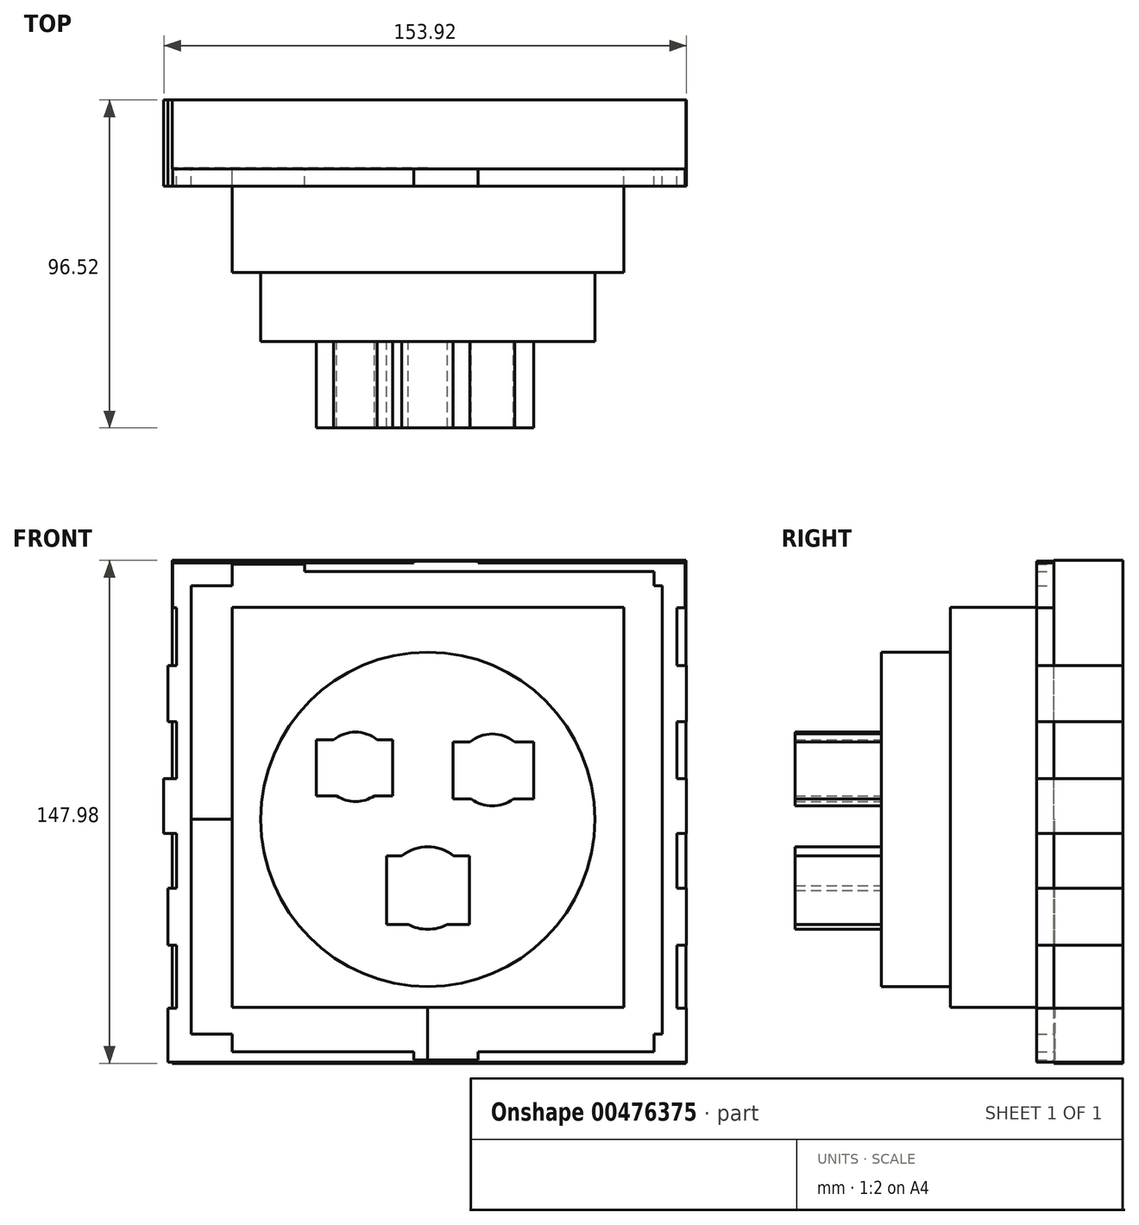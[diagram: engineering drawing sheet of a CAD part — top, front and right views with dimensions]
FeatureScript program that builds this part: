
annotation { "Feature Type Name" : "Feature", "Feature Type Description" : "" }
export const myFeature = defineFeature(function(context is Context, id is Id, definition is map)
    precondition{}
    {
        {
            var Q0;
            Q0=qCreatedBy(makeId("Front.planeOp"),FACE);
            var sketch = newSketch(context, id + "F0", { "sketchPlane" : qUnion([Q0])});
            skLineSegment(sketch, "E0.bottom", {"start": v(-76.5, 45.26) * mm, "end": v(76.2, 45.26) * mm});
            skLineSegment(sketch, "E0.top", {"start": v(-76.5, 28.8) * mm, "end": v(76.2, 28.8) * mm});
            skLineSegment(sketch, "E0.left", {"start": v(-76.5, 45.26) * mm, "end": v(-76.5, 28.8) * mm});
            skLineSegment(sketch, "E0.right", {"start": v(76.2, 45.26) * mm, "end": v(76.2, 28.8) * mm});
            skLineSegment(sketch, "E1.bottom", {"start": v(-77.72, 12.04) * mm, "end": v(76.2, 12.04) * mm});
            skLineSegment(sketch, "E1.top", {"start": v(-77.72, -4.11) * mm, "end": v(76.2, -4.11) * mm});
            skLineSegment(sketch, "E1.left", {"start": v(-77.72, 12.04) * mm, "end": v(-77.72, -4.11) * mm});
            skLineSegment(sketch, "E1.right", {"start": v(76.2, 12.04) * mm, "end": v(76.2, -4.11) * mm});
            skLineSegment(sketch, "E2.bottom", {"start": v(-76.5, -20.27) * mm, "end": v(76.2, -20.27) * mm});
            skLineSegment(sketch, "E2.top", {"start": v(-76.5, -37.03) * mm, "end": v(76.2, -37.03) * mm});
            skLineSegment(sketch, "E2.left", {"start": v(-76.5, -20.27) * mm, "end": v(-76.5, -37.03) * mm});
            skLineSegment(sketch, "E2.right", {"start": v(76.2, -20.27) * mm, "end": v(76.2, -37.03) * mm});
            skLineSegment(sketch, "E3.bottom", {"start": v(-76.5, -55.63) * mm, "end": v(76.2, -55.63) * mm});
            skLineSegment(sketch, "E3.top", {"start": v(-76.5, -71.48) * mm, "end": v(76.2, -71.48) * mm});
            skLineSegment(sketch, "E3.left", {"start": v(-76.5, -55.63) * mm, "end": v(-76.5, -71.48) * mm});
            skLineSegment(sketch, "E3.right", {"start": v(76.2, -55.63) * mm, "end": v(76.2, -71.48) * mm});
            skLineSegment(sketch, "E4.bottom", {"start": v(-57.6, 75.13) * mm, "end": v(-36.27, 75.13) * mm});
            skLineSegment(sketch, "E4.top", {"start": v(-57.6, -71.48) * mm, "end": v(-36.27, -71.48) * mm});
            skLineSegment(sketch, "E4.left", {"start": v(-57.6, 75.13) * mm, "end": v(-57.6, -71.48) * mm});
            skLineSegment(sketch, "E4.right", {"start": v(-36.27, 75.13) * mm, "end": v(-36.27, -71.48) * mm});
            skLineSegment(sketch, "E5.bottom", {"start": v(-4.11, -70.87) * mm, "end": v(14.78, -70.87) * mm});
            skLineSegment(sketch, "E5.top", {"start": v(-4.11, 76.05) * mm, "end": v(14.78, 76.05) * mm});
            skLineSegment(sketch, "E5.left", {"start": v(-4.11, -70.87) * mm, "end": v(-4.11, 76.05) * mm});
            skLineSegment(sketch, "E5.right", {"start": v(14.78, -70.87) * mm, "end": v(14.78, 76.05) * mm});
            skLineSegment(sketch, "E6.bottom", {"start": v(49.53, -71.48) * mm, "end": v(66.6, -71.48) * mm});
            skLineSegment(sketch, "E6.top", {"start": v(49.53, 75.44) * mm, "end": v(66.6, 75.44) * mm});
            skLineSegment(sketch, "E6.left", {"start": v(49.53, -71.48) * mm, "end": v(49.53, 75.44) * mm});
            skLineSegment(sketch, "E6.right", {"start": v(66.6, -71.48) * mm, "end": v(66.6, 75.44) * mm});
            skLineSegment(sketch, "E7.bottom", {"start": v(-75.13, 62.33) * mm, "end": v(75.74, 62.33) * mm});
            skLineSegment(sketch, "E7.top", {"start": v(-75.13, 75.44) * mm, "end": v(75.74, 75.44) * mm});
            skLineSegment(sketch, "E7.left", {"start": v(-75.13, 62.33) * mm, "end": v(-75.13, 75.44) * mm});
            skLineSegment(sketch, "E7.right", {"start": v(75.74, 62.33) * mm, "end": v(75.74, 75.44) * mm});
            skLineSegment(sketch, "E8.bottom", {"start": v(73.3, 73) * mm, "end": v(-73.91, 73) * mm});
            skLineSegment(sketch, "E8.top", {"start": v(73.3, -68.43) * mm, "end": v(-73.91, -68.43) * mm});
            skLineSegment(sketch, "E8.left", {"start": v(73.3, 73) * mm, "end": v(73.3, -68.43) * mm});
            skLineSegment(sketch, "E8.right", {"start": v(-73.91, 73) * mm, "end": v(-73.91, -68.43) * mm});
            skLineSegment(sketch, "E9.bottom", {"start": v(69.04, 68.73) * mm, "end": v(-69.65, 68.73) * mm});
            skLineSegment(sketch, "E9.top", {"start": v(69.04, -63.25) * mm, "end": v(-69.65, -63.25) * mm});
            skLineSegment(sketch, "E9.left", {"start": v(69.04, 68.73) * mm, "end": v(69.04, -63.25) * mm});
            skLineSegment(sketch, "E9.right", {"start": v(-69.65, 68.73) * mm, "end": v(-69.65, -63.25) * mm});
            skCircle(sketch, "E10", {"center": v(45.57, 56.54) * mm, "radius": 3.05 * mm});
            skCircle(sketch, "E11", {"center": v(17.83, 56.54) * mm, "radius": 3.05 * mm});
            skCircle(sketch, "E12", {"center": v(-9, 56.24) * mm, "radius": 3.05 * mm});
            skCircle(sketch, "E13", {"center": v(-31.55, 56.24) * mm, "radius": 3 * mm});
            skCircle(sketch, "E14", {"center": v(-49.23, 55.93) * mm, "radius": 3.18 * mm});
            skCircle(sketch, "E15", {"center": v(45.57, 19.66) * mm, "radius": 3.28 * mm});
            skCircle(sketch, "E16", {"center": v(18.14, 19.35) * mm, "radius": 3.35 * mm});
            skCircle(sketch, "E17", {"center": v(-8.38, 19.66) * mm, "radius": 3.18 * mm});
            skCircle(sketch, "E18", {"center": v(-29.1, 19.05) * mm, "radius": 3.24 * mm});
            skCircle(sketch, "E19", {"center": v(-51.97, 17.83) * mm, "radius": 3.1 * mm});
            skCircle(sketch, "E20", {"center": v(46.18, -12.95) * mm, "radius": 3.14 * mm});
            skCircle(sketch, "E21", {"center": v(19.66, -12.95) * mm, "radius": 2.6 * mm});
            skCircle(sketch, "E22", {"center": v(-8.69, -12.65) * mm, "radius": 3 * mm});
            skCircle(sketch, "E23", {"center": v(-30.94, -13.26) * mm, "radius": 3.24 * mm});
            skCircle(sketch, "E24", {"center": v(-54.1, -12.95) * mm, "radius": 3.5 * mm});
            skCircle(sketch, "E25", {"center": v(46.48, -46.18) * mm, "radius": 2.81 * mm});
            skCircle(sketch, "E26", {"center": v(20.57, -46.48) * mm, "radius": 3.06 * mm});
            skCircle(sketch, "E27", {"center": v(-9.3, -46.79) * mm, "radius": 3.18 * mm});
            skCircle(sketch, "E28", {"center": v(-30.94, -47.4) * mm, "radius": 3.05 * mm});
            skCircle(sketch, "E29", {"center": v(-51.66, -47.7) * mm, "radius": 3.14 * mm});
            skSolve(sketch);
        }
        {
            var Q0;
            Q0=qCreatedBy(makeId("Front.planeOp"),FACE);
            var sketch = newSketch(context, id + "F1", { "sketchPlane" : qUnion([Q0])});
            skLineSegment(sketch, "E30.bottom", {"start": v(-75.28, 76.2) * mm, "end": v(76.05, 76.2) * mm});
            skLineSegment(sketch, "E30.top", {"start": v(-75.28, -71.78) * mm, "end": v(76.05, -71.78) * mm});
            skLineSegment(sketch, "E30.left", {"start": v(-75.28, 76.2) * mm, "end": v(-75.28, -71.78) * mm});
            skLineSegment(sketch, "E30.right", {"start": v(76.05, 76.2) * mm, "end": v(76.05, -71.78) * mm});
            skSolve(sketch);
        }
        {
            var Q0;
            Q0=qSketchRegion(id+"F1",true);
            extrude(context, id + "F2", {"entities" : qUnion([Q0]), "depth" : 20.07 * mm});
        }
        {
            var Q0;
            Q0=makeQuery(id+"F2.opExtrude","CAP_FACE",FACE,{"disambiguationData":[OSD([sQuery(id+"F1.wireOp",EDGE,"E30.bottom"),sQuery(id+"F1.wireOp",EDGE,"E30.top"),sQuery(id+"F1.wireOp",EDGE,"E30.left"),sQuery(id+"F1.wireOp",EDGE,"E30.right")])],"isStart":false});
            var sketch = newSketch(context, id + "F3", { "sketchPlane" : qUnion([Q0])});
            skLineSegment(sketch, "E31.bottom", {"start": v(-75.28, 76.2) * mm, "end": v(0, 76.2) * mm});
            skLineSegment(sketch, "E31.top", {"start": v(-75.28, 0) * mm, "end": v(0, 0) * mm});
            skLineSegment(sketch, "E31.left", {"start": v(-75.28, 76.2) * mm, "end": v(-75.28, 0) * mm});
            skLineSegment(sketch, "E31.right", {"start": v(0, 76.2) * mm, "end": v(0, 0) * mm});
            skLineSegment(sketch, "E32.bottom", {"start": v(0, 0) * mm, "end": v(76.05, 0) * mm});
            skLineSegment(sketch, "E32.top", {"start": v(0, 76.2) * mm, "end": v(76.05, 76.2) * mm});
            skLineSegment(sketch, "E32.left", {"start": v(0, 0) * mm, "end": v(0, 76.2) * mm});
            skLineSegment(sketch, "E32.right", {"start": v(76.05, 0) * mm, "end": v(76.05, 76.2) * mm});
            skLineSegment(sketch, "E33.bottom", {"start": v(0, 0) * mm, "end": v(-75.28, 0) * mm});
            skLineSegment(sketch, "E33.top", {"start": v(0, -71.78) * mm, "end": v(-75.28, -71.78) * mm});
            skLineSegment(sketch, "E33.left", {"start": v(0, 0) * mm, "end": v(0, -71.78) * mm});
            skLineSegment(sketch, "E33.right", {"start": v(-75.28, 0) * mm, "end": v(-75.28, -71.78) * mm});
            skLineSegment(sketch, "E34.top", {"start": v(0, -71.78) * mm, "end": v(76.05, -71.78) * mm});
            skLineSegment(sketch, "E34.right", {"start": v(76.05, 0) * mm, "end": v(76.05, -71.78) * mm});
            skSolve(sketch);
        }
        {
            var Q0;
            Q0=makeQuery(id+"F3.imprint","IMPRINT",FACE,{"disambiguationData":[TD([[makeQuery(id+"F3.imprint","IMPRINT",EDGE,{"derivedFrom":sQuery(id+"F3.wireOp",EDGE,"E31.bottom")}),-1.0]])]});
            var Q1;
            Q1=makeQuery(id+"F3.imprint","IMPRINT",FACE,{"disambiguationData":[TD([[makeQuery(id+"F3.imprint","IMPRINT",EDGE,{"derivedFrom":sQuery(id+"F3.wireOp",EDGE,"E33.bottom")}),1.0]])]});
            var Q2;
            Q2=makeQuery(id+"F3.imprint","IMPRINT",FACE,{"disambiguationData":[TD([[makeQuery(id+"F3.imprint","IMPRINT",EDGE,{"derivedFrom":sQuery(id+"F3.wireOp",EDGE,"E32.bottom")}),-1.0]])]});
            var Q3;
            Q3=makeQuery(id+"F3.imprint","IMPRINT",FACE,{"disambiguationData":[TD([[makeQuery(id+"F3.imprint","IMPRINT",EDGE,{"derivedFrom":sQuery(id+"F3.wireOp",EDGE,"E32.top")}),-1.0]])]});
            extrude(context, id + "F4", {"entities" : qUnion([Q0, Q1, Q2, Q3]), "operationType" : NewBodyOperationType.ADD, "depth" : 0.25 * mm});
        }
        {
            var Q0;
            Q0=makeQuery(id+"F4.opExtrude","CAP_FACE",FACE,{"disambiguationData":[OSD([sQuery(id+"F3.wireOp",EDGE,"E31.bottom"),sQuery(id+"F3.wireOp",EDGE,"E31.left"),sQuery(id+"F3.wireOp",EDGE,"E32.top"),sQuery(id+"F3.wireOp",EDGE,"E32.right"),sQuery(id+"F3.wireOp",EDGE,"E33.top"),sQuery(id+"F3.wireOp",EDGE,"E33.right"),sQuery(id+"F3.wireOp",EDGE,"E34.top"),sQuery(id+"F3.wireOp",EDGE,"E34.right")])],"isStart":false});
            var sketch = newSketch(context, id + "F5", { "sketchPlane" : qUnion([Q0])});
            skCircle(sketch, "E35", {"center": v(0, 0) * mm, "radius": 49.2 * mm});
            skSolve(sketch);
        }
        {
            var Q0;
            Q0=qSketchRegion(id+"F5",true);
            extrude(context, id + "F6", {"entities" : qUnion([Q0]), "operationType" : NewBodyOperationType.ADD, "depth" : 25.4 * mm});
        }
        {
            var Q0;
            Q0=makeQuery(id+"F6.opExtrude","CAP_FACE",FACE,{"disambiguationData":[OSD([sQuery(id+"F5.wireOp",EDGE,"E35")])],"isStart":false});
            var sketch = newSketch(context, id + "F7", { "sketchPlane" : qUnion([Q0])});
            skArc(sketch, "E36", {"start": v(-52.7, 45.38) * mm, "mid": v(52.15, -40.45) * mm, "end": v(-51.18, 47.21) * mm});
            skSolve(sketch);
        }
        {
            var Q0;
            Q0=makeQuery(id+"F7.imprint","IMPRINT",FACE,{"disambiguationData":[TD([[makeQuery(id+"F7.imprint","IMPRINT",EDGE,{"derivedFrom":makeQuery(id+"F6.opExtrude","CAP_EDGE",EDGE,{"disambiguationData":[OSD([sQuery(id+"F5.wireOp",EDGE,"E35")])],"isStart":false})}),1.0]])]});
            extrude(context, id + "F8", {"entities" : qUnion([Q0]), "operationType" : NewBodyOperationType.ADD, "depth" : 25.4 * mm});
        }
        {
            var Q0;
            Q0=makeQuery(id+"F4.opExtrude","CAP_FACE",FACE,{"disambiguationData":[OSD([sQuery(id+"F3.wireOp",EDGE,"E31.bottom"),sQuery(id+"F3.wireOp",EDGE,"E31.left"),sQuery(id+"F3.wireOp",EDGE,"E32.top"),sQuery(id+"F3.wireOp",EDGE,"E32.right"),sQuery(id+"F3.wireOp",EDGE,"E33.top"),sQuery(id+"F3.wireOp",EDGE,"E33.right"),sQuery(id+"F3.wireOp",EDGE,"E34.top"),sQuery(id+"F3.wireOp",EDGE,"E34.right")])],"isStart":false});
            var sketch = newSketch(context, id + "F9", { "sketchPlane" : qUnion([Q0])});
            skCircle(sketch, "E37", {"center": v(0, 0) * mm, "radius": 70.77 * mm});
            skSolve(sketch);
        }
        {
            var Q0;
            Q0=qCreatedBy(makeId("Front.planeOp"),FACE);
            var sketch = newSketch(context, id + "F10", { "sketchPlane" : qUnion([Q0])});
            skCircle(sketch, "E38", {"center": v(45.23, 56.98) * mm, "radius": 3.19 * mm});
            skCircle(sketch, "E39", {"center": v(18.08, 56.67) * mm, "radius": 3.48 * mm});
            skCircle(sketch, "E40", {"center": v(-8.77, 56.67) * mm, "radius": 3.56 * mm});
            skCircle(sketch, "E41", {"center": v(-31.65, 56.67) * mm, "radius": 2.88 * mm});
            skCircle(sketch, "E42", {"center": v(-49.35, 56.67) * mm, "radius": 2.46 * mm});
            skCircle(sketch, "E43", {"center": v(45.84, 20.06) * mm, "radius": 3.37 * mm});
            skCircle(sketch, "E44", {"center": v(18.08, 19.15) * mm, "radius": 3.48 * mm});
            skCircle(sketch, "E45", {"center": v(-8.16, 20.06) * mm, "radius": 3.11 * mm});
            skCircle(sketch, "E46", {"center": v(-28.9, 19.15) * mm, "radius": 3.14 * mm});
            skCircle(sketch, "E47", {"center": v(-52.4, 18.23) * mm, "radius": 3.24 * mm});
            skCircle(sketch, "E48", {"center": v(46.45, -12.9) * mm, "radius": 3.57 * mm});
            skCircle(sketch, "E49", {"center": v(19.6, -12.59) * mm, "radius": 2.62 * mm});
            skCircle(sketch, "E50", {"center": v(-8.47, -12.59) * mm, "radius": 3.37 * mm});
            skCircle(sketch, "E51", {"center": v(-31.04, -13.2) * mm, "radius": 3.48 * mm});
            skCircle(sketch, "E52", {"center": v(-52.4, -12.28) * mm, "radius": 3.48 * mm});
            skCircle(sketch, "E53", {"center": v(46.45, -45.84) * mm, "radius": 3.41 * mm});
            skCircle(sketch, "E54", {"center": v(20.52, -45.54) * mm, "radius": 2.73 * mm});
            skCircle(sketch, "E55", {"center": v(-10.3, -46.76) * mm, "radius": 3.3 * mm});
            skCircle(sketch, "E56", {"center": v(-31.65, -47.06) * mm, "radius": 4.01 * mm});
            skCircle(sketch, "E57", {"center": v(-52.4, -47.37) * mm, "radius": 3.48 * mm});
            skSolve(sketch);
        }
        {
            var Q0;
            Q0=qSketchRegion(id+"F10",true);
            extrude(context, id + "F11", {"entities" : qUnion([Q0]), "operationType" : NewBodyOperationType.ADD, "depth" : 25.4 * mm});
        }
        {
            var Q0;
            Q0=qSketchRegion(id+"F0",true);
            extrude(context, id + "F12", {"entities" : qUnion([Q0]), "operationType" : NewBodyOperationType.ADD, "depth" : 25.4 * mm});
        }
        {
            var Q0;
            Q0=qCreatedBy(makeId("Front.planeOp"),FACE);
            var sketch = newSketch(context, id + "F13", { "sketchPlane" : qUnion([Q0])});
            skLineSegment(sketch, "E58.bottom", {"start": v(-57.59, 62.47) * mm, "end": v(57.74, 62.47) * mm});
            skLineSegment(sketch, "E58.top", {"start": v(-57.59, -55.3) * mm, "end": v(57.74, -55.3) * mm});
            skLineSegment(sketch, "E58.left", {"start": v(-57.59, 62.47) * mm, "end": v(-57.59, -55.3) * mm});
            skLineSegment(sketch, "E58.right", {"start": v(57.74, 62.47) * mm, "end": v(57.74, -55.3) * mm});
            skSolve(sketch);
        }
        {
            var Q0;
            Q0=qSketchRegion(id+"F13",true);
            extrude(context, id + "F14", {"entities" : qUnion([Q0]), "operationType" : NewBodyOperationType.ADD, "depth" : 50.8 * mm});
        }
        {
            var Q0;
            Q0=makeQuery(id+"F8.opExtrude","CAP_FACE",FACE,{"disambiguationData":[OSD([sQuery(id+"F5.wireOp",EDGE,"E35")])],"isStart":false});
            var sketch = newSketch(context, id + "F15", { "sketchPlane" : qUnion([Q0])});
            skCircle(sketch, "E59", {"center": v(-21.28, 15.48) * mm, "radius": 10.2 * mm});
            skCircle(sketch, "E60", {"center": v(19, 14.57) * mm, "radius": 10.57 * mm});
            skCircle(sketch, "E61", {"center": v(0, -20.21) * mm, "radius": 12.15 * mm});
            skSolve(sketch);
        }
        {
            var Q0;
            Q0 = qSketchRegion(id + "F15", true);
            extrude(context, id + "F16", {"entities" : qUnion([Q0]), "operationType" : NewBodyOperationType.ADD, "depth" : 25.4 * mm});
        }
        {
            var Q0;
            Q0=makeQuery(id+"F8.opExtrude","CAP_FACE",FACE,{"disambiguationData":[OSD([sQuery(id+"F5.wireOp",EDGE,"E35")])],"isStart":false});
            var sketch = newSketch(context, id + "F17", { "sketchPlane" : qUnion([Q0])});
            skLineSegment(sketch, "E62.bottom", {"start": v(-32.87, 23.42) * mm, "end": v(-10.3, 23.42) * mm});
            skLineSegment(sketch, "E62.top", {"start": v(-32.87, 6.94) * mm, "end": v(-10.3, 6.94) * mm});
            skLineSegment(sketch, "E62.left", {"start": v(-32.87, 23.42) * mm, "end": v(-32.87, 6.94) * mm});
            skLineSegment(sketch, "E62.right", {"start": v(-10.3, 23.42) * mm, "end": v(-10.3, 6.94) * mm});
            skLineSegment(sketch, "E63.bottom", {"start": v(7.4, 22.8) * mm, "end": v(31.2, 22.8) * mm});
            skLineSegment(sketch, "E63.top", {"start": v(7.4, 6.03) * mm, "end": v(31.2, 6.03) * mm});
            skLineSegment(sketch, "E63.left", {"start": v(7.4, 22.8) * mm, "end": v(7.4, 6.03) * mm});
            skLineSegment(sketch, "E63.right", {"start": v(31.2, 22.8) * mm, "end": v(31.2, 6.03) * mm});
            skLineSegment(sketch, "E64.bottom", {"start": v(-12.13, -10.76) * mm, "end": v(12.28, -10.76) * mm});
            skLineSegment(sketch, "E64.top", {"start": v(-12.13, -30.9) * mm, "end": v(12.28, -30.9) * mm});
            skLineSegment(sketch, "E64.left", {"start": v(-12.13, -10.76) * mm, "end": v(-12.13, -30.9) * mm});
            skLineSegment(sketch, "E64.right", {"start": v(12.28, -10.76) * mm, "end": v(12.28, -30.9) * mm});
            skSolve(sketch);
        }
        {
            var Q0;
            Q0 = qSketchRegion(id + "F17", true);
            extrude(context, id + "F18", {"entities" : qUnion([Q0]), "operationType" : NewBodyOperationType.ADD, "depth" : 25.4 * mm});
        }
    });
